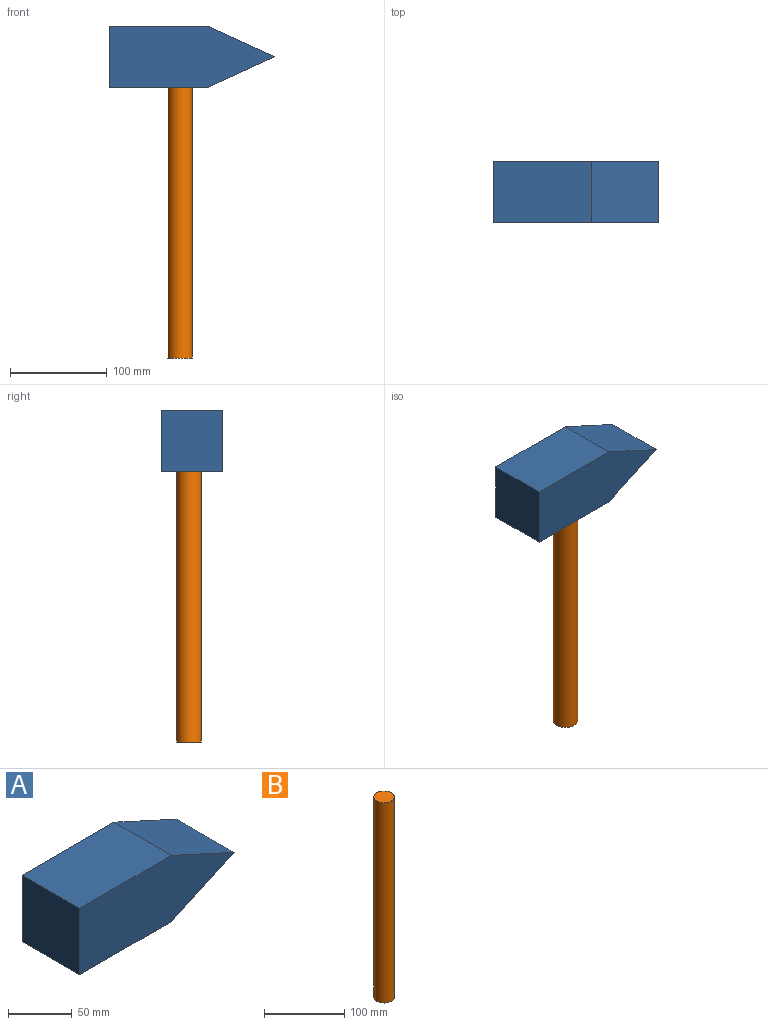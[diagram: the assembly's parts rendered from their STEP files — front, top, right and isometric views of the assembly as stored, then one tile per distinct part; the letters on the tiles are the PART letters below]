
ASSEMBLY  parts=2 mates=1
PART A: 9 faces, bbox 170.9x63.5x63.5 mm
  f0: plane 63.5x63.5mm, normal (-1,0,0), area 4032.3mm2, adj f1,f4,f5,f6
  f1: plane 101.6x63.5mm, normal (0,0,-1), area 5944.9mm2, adj f0,f2,f5,f6,f7
  f2: plane 69.27x63.5mm, normal (0.42,0,-0.91), area 4838.7mm2, adj f1,f3,f5,f6
  f3: plane 69.27x63.5mm, normal (0.42,0,0.91), area 4838.7mm2, adj f2,f4,f5,f6
  f4: plane 101.6x63.5mm, normal (0,0,1), area 6451.6mm2, adj f0,f3,f5,f6
  f5: plane 170.87x63.5mm, normal (0,-1,0), area 8650.9mm2, adj f0,f1,f2,f3,f4
  f6: plane 170.87x63.5mm, normal (0,1,0), area 8650.9mm2, adj f0,f1,f2,f3,f4
  f7: cylinder r=12.7mm len=25.4mm, axis (0,0,-1), area 2026.8mm2, adj f1,f8
  f8: plane 25.4x25.4mm, normal (0,0,-1), area 506.7mm2, adj f7
PART B: 3 faces, bbox 25.4x25.4x304.8 mm
  f0: cylinder r=12.7mm len=304.8mm, axis (0,0,-1), area 24322mm2, adj f1,f2
  f1: plane 25.4x25.4mm, normal (0,0,1), area 506.7mm2, adj f0
  f2: plane 25.4x25.4mm, normal (0,0,-1), area 506.7mm2, adj f0
PLACE A t=(-48.99,133.22,88.9)mm
PLACE B t=(24.04,104.65,-190.5)mm
MATE fastened B.f0 <-> A.f7  axis (0,0,1) through (24.04,104.65,114.3)mm
